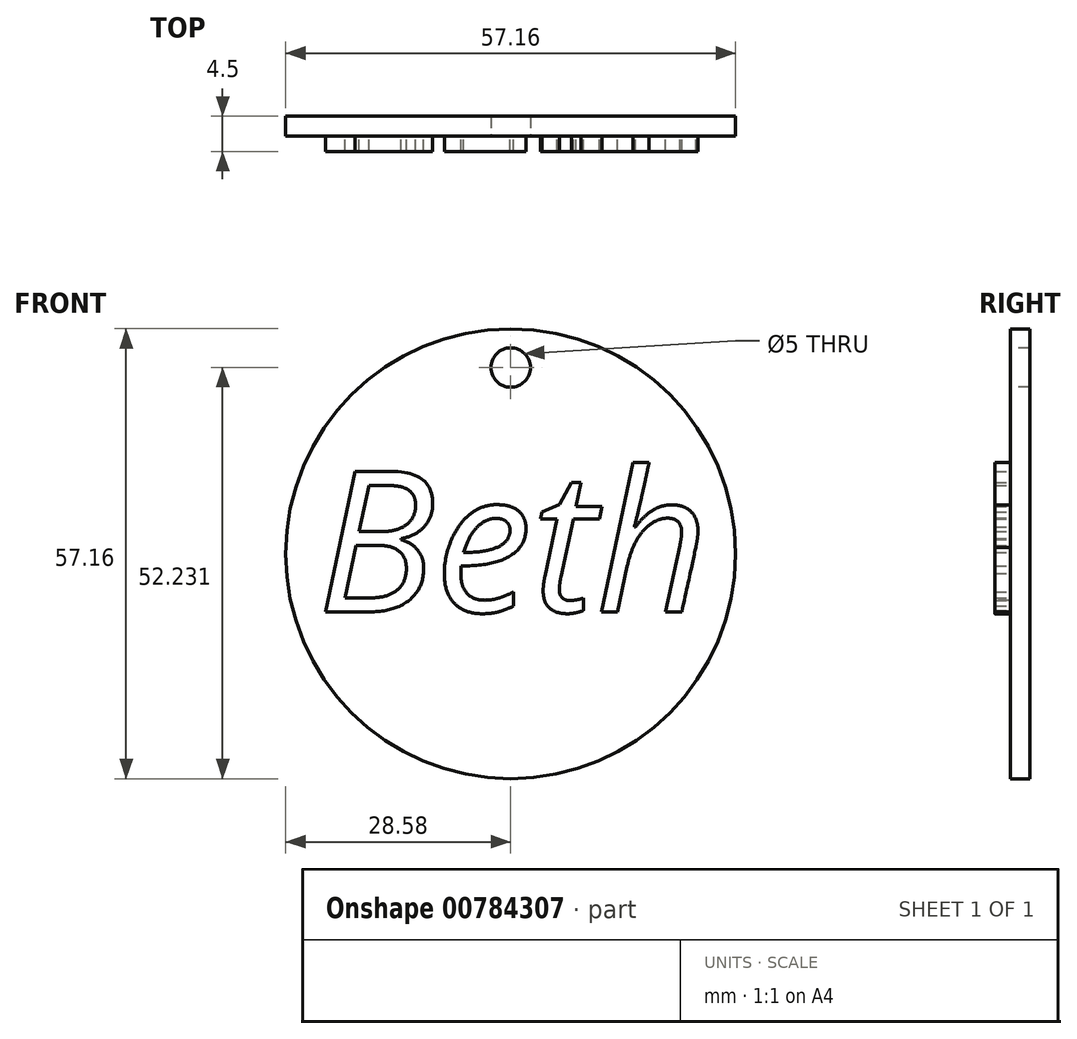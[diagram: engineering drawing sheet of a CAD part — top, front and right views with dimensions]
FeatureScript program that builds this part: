
annotation { "Feature Type Name" : "Feature", "Feature Type Description" : "" }
export const myFeature = defineFeature(function(context is Context, id is Id, definition is map)
    precondition{}
    {
        {
            var Q0;
            Q0=qCreatedBy(makeId("Front.planeOp"),FACE);
            var sketch = newSketch(context, id + "F0", { "sketchPlane" : qUnion([Q0])});
            skCircle(sketch, "E0", {"center": v(0, 0) * mm, "radius": 28.57 * mm});
            skSolve(sketch);
        }
        {
            var Q0;
            Q0 = qSketchRegion(id + "F0", true);
            extrude(context, id + "F1", {"entities" : qUnion([Q0]), "depth" : 2.5 * mm, "offsetDistance" : 25.4 * mm, "symmetric" : true});
        }
        {
            var Q0;
            Q0=makeQuery(id+"F1.opExtrude","CAP_FACE",FACE,{"disambiguationData":[OSD([sQuery(id+"F0.wireOp",EDGE,"E0")])],"isStart":false});
            var sketch = newSketch(context, id + "F2", { "sketchPlane" : qUnion([Q0])});
            skText(sketch, "E1", { "text": "Beth\n", "fontName": "OpenSans-Italic.ttf"});
            const initialGuessF2  = {"E1": [-0.02457, -0.00738, 1, 0, 0.01799]};
            skSetInitialGuess(sketch, initialGuessF2);
            skSolve(sketch);
        }
        {
            var Q0;
            Q0 = qSketchRegion(id + "F2", true);
            extrude(context, id + "F3", {"entities" : qUnion([Q0]), "operationType" : NewBodyOperationType.ADD, "depth" : 2 * mm, "offsetDistance" : 25.4 * mm});
        }
        {
            var Q0;
            {var subQ0=sQuery(id+"F0.wireOp",EDGE,"E0");Q0=makeQuery(id+"F3.boolean.opBoolean","SPLIT",FACE,{"disambiguationData":[TD([makeQuery(id+"F1.opExtrude","SWEPT_FACE",FACE,{"disambiguationData":[OSD([subQ0])]})])],"derivedFrom":makeQuery(id+"F1.opExtrude","CAP_FACE",FACE,{"disambiguationData":[OSD([subQ0])],"isStart":false})});}
            var sketch = newSketch(context, id + "F4", { "sketchPlane" : qUnion([Q0])});
            skCircle(sketch, "E2", {"center": v(0, 23.65) * mm, "radius": 2.57 * mm});
            skSolve(sketch);
        }
        {
            var Q0;
            Q0=sQuery(id+"F4.wireOp",VERTEX,"E2.center");
            var Q1;
            Q1=makeQuery(id+"F1.opExtrude","SWEPT_BODY",BODY,{"disambiguationData":[OSD([sQuery(id+"F0.wireOp",EDGE,"E0")])]});
            hole(context, id + "F5", {"style" : HoleStyle.SIMPLE, "endStyle" : HoleEndStyle.THROUGH, "holeDiameter" : 5 * mm, "majorDiameter" : 5 * mm, "isTappedThrough" : true, "tappedDepth" : 12 * mm, "tapClearance" : 3, "locations" : qUnion([Q0]), "scope" : qUnion([Q1])});
        }
    });
